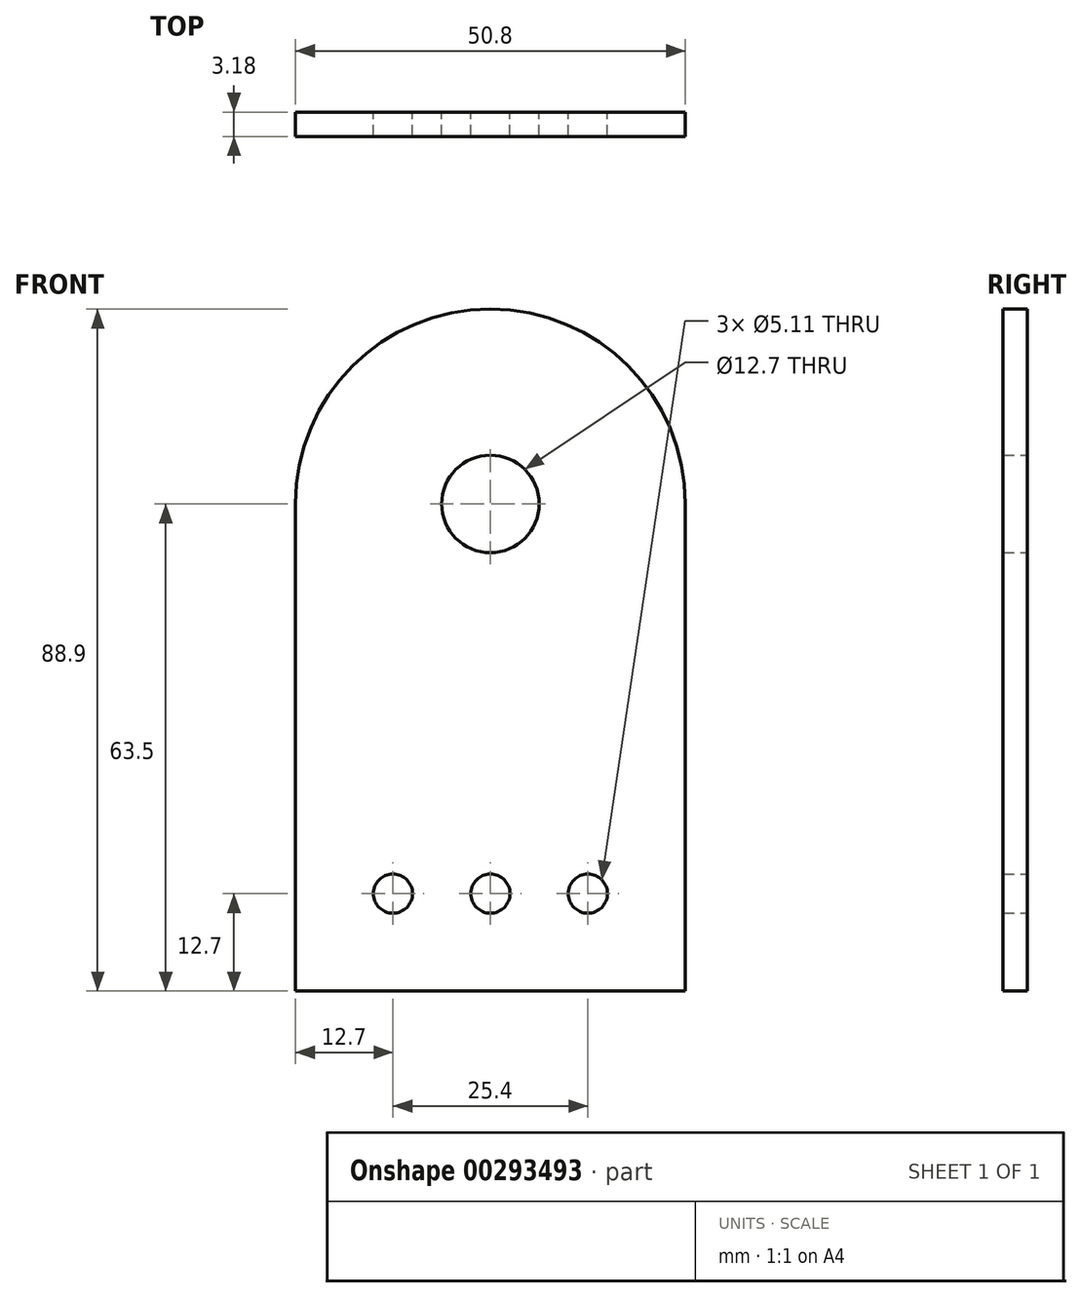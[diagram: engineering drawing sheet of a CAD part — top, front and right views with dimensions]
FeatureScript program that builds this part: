
annotation { "Feature Type Name" : "Feature", "Feature Type Description" : "" }
export const myFeature = defineFeature(function(context is Context, id is Id, definition is map)
    precondition{}
    {
        {
            var Q0;
            Q0=qCreatedBy(makeId("Front.planeOp"),FACE);
            var sketch = newSketch(context, id + "F0", { "sketchPlane" : qUnion([Q0])});
            skCircle(sketch, "E0", {"center": v(0, 0) * mm, "radius": 6.35 * mm});
            skArc(sketch, "E1", {"start": v(25.4, 0) * mm, "mid": v(0, 25.4) * mm, "end": v(-25.4, 0) * mm});
            skLineSegment(sketch, "E2", {"start": v(-25.4, 0) * mm, "end": v(-25.4, -63.5) * mm});
            skLineSegment(sketch, "E3", {"start": v(-25.4, -63.5) * mm, "end": v(25.4, -63.5) * mm});
            skLineSegment(sketch, "E4", {"start": v(25.4, -63.5) * mm, "end": v(25.4, 0) * mm});
            skCircle(sketch, "E5", {"center": v(-12.7, -50.8) * mm, "radius": 2.55 * mm});
            skCircle(sketch, "E6.1.0.0", {"center": v(0, -50.8) * mm, "radius": 2.55 * mm});
            skCircle(sketch, "E6.2.0.0", {"center": v(12.7, -50.8) * mm, "radius": 2.55 * mm});
            skLineSegment(sketch, "E6.direction1", {"start": v(-12.7, -50.8) * mm, "end": v(0, -50.8) * mm, "construction": true});
            skSolve(sketch);
        }
        {
            var Q0;
            Q0=makeQuery(id+"F0.imprint","IMPRINT",FACE,{"disambiguationData":[TD([[makeQuery(id+"F0.imprint","IMPRINT",EDGE,{"derivedFrom":sQuery(id+"F0.wireOp",EDGE,"E0")}),-1.0]])]});
            extrude(context, id + "F1", {"entities" : qUnion([Q0]), "depth" : 3.17 * mm});
        }
    });
